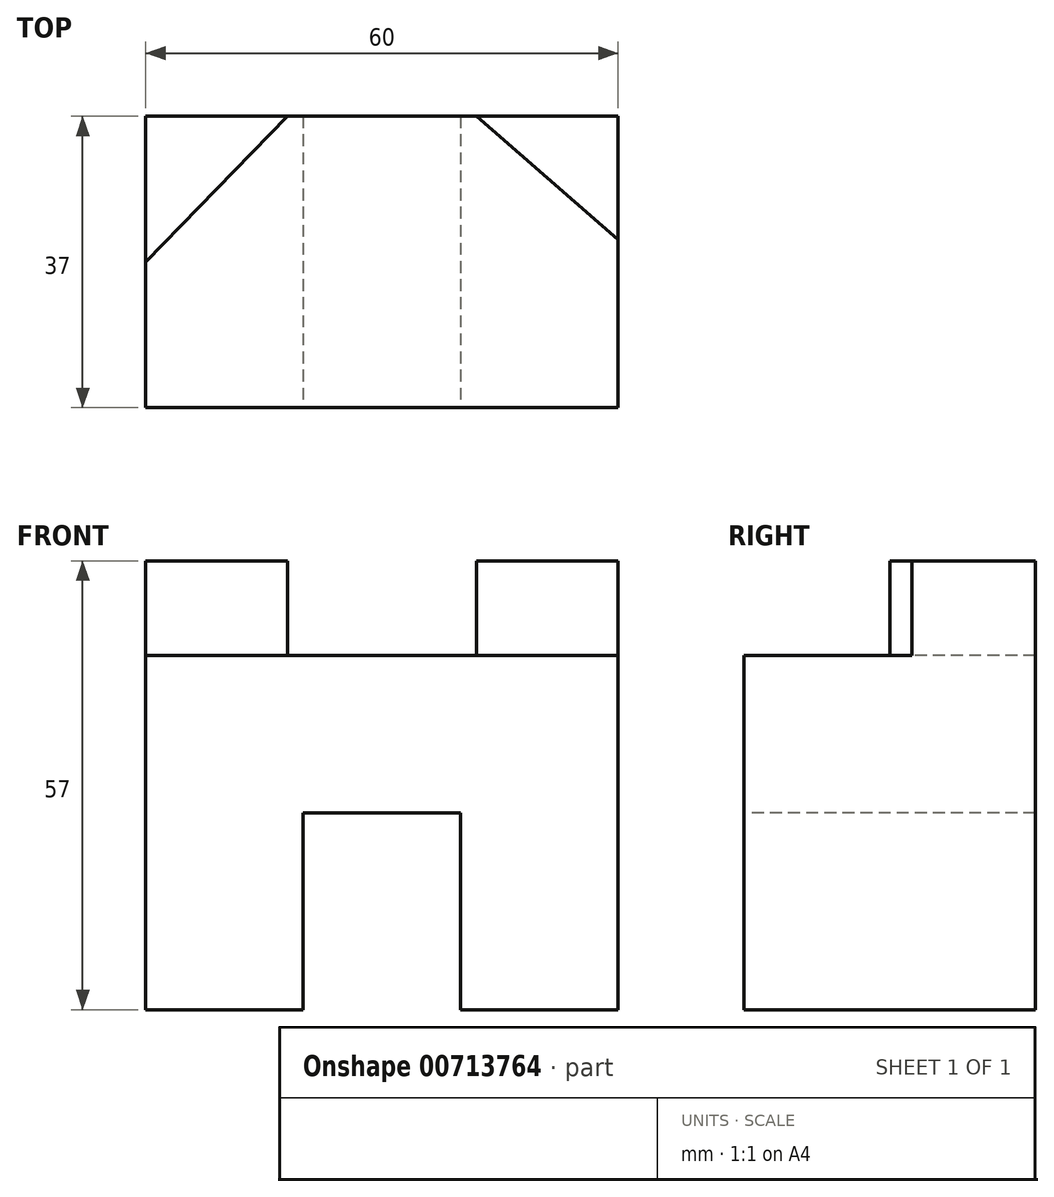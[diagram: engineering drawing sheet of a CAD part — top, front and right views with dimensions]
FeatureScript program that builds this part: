
annotation { "Feature Type Name" : "Feature", "Feature Type Description" : "" }
export const myFeature = defineFeature(function(context is Context, id is Id, definition is map)
    precondition{}
    {
        {
            var Q0;
            Q0=qCreatedBy(makeId("Front.planeOp"),FACE);
            var sketch = newSketch(context, id + "F0", { "sketchPlane" : qUnion([Q0])});
            skLineSegment(sketch, "E0.bottom", {"start": v(30, -28.5) * mm, "end": v(-30, -28.5) * mm});
            skLineSegment(sketch, "E0.top", {"start": v(30, 28.5) * mm, "end": v(-30, 28.5) * mm});
            skLineSegment(sketch, "E0.left", {"start": v(30, -28.5) * mm, "end": v(30, 28.5) * mm});
            skLineSegment(sketch, "E0.right", {"start": v(-30, -28.5) * mm, "end": v(-30, 28.5) * mm});
            skPoint(sketch, "E0.middle", {"position": v(0, 0) * mm});
            skLineSegment(sketch, "E1.left", {"start": v(12.78, -28.5) * mm, "end": v(12.78, -28.5) * mm});
            skLineSegment(sketch, "E1.right", {"start": v(-12.78, -28.5) * mm, "end": v(-12.78, -28.5) * mm});
            skPoint(sketch, "E1.middle", {"position": v(0, -28.5) * mm});
            skSolve(sketch);
        }
        {
            var Q0;
            Q0 = qSketchRegion(id + "F0", true);
            extrude(context, id + "F1", {"entities" : qUnion([Q0]), "depth" : 37 * mm, "offsetDistance" : 25 * mm});
        }
        {
            var Q0;
            Q0=makeQuery(id+"F1.opExtrude","SWEPT_FACE",FACE,{"disambiguationData":[OSD([sQuery(id+"F0.wireOp",EDGE,"E0.top")])]});
            var sketch = newSketch(context, id + "F2", { "sketchPlane" : qUnion([Q0])});
            skLineSegment(sketch, "E2", {"start": v(-12, 0) * mm, "end": v(-30, -18.5) * mm});
            skLineSegment(sketch, "E3", {"start": v(-30, -18.5) * mm, "end": v(-30, 0) * mm});
            skLineSegment(sketch, "E4", {"start": v(-30, 0) * mm, "end": v(-12, 0) * mm});
            skLineSegment(sketch, "E5", {"start": v(30, 0) * mm, "end": v(30, -15.7) * mm});
            skLineSegment(sketch, "E6", {"start": v(30, -15.7) * mm, "end": v(12, 0) * mm});
            skSolve(sketch);
        }
        {
            var Q0;
            {var subQ3=sQuery(id+"F2.wireOp",EDGE,"E2");Q0=makeQuery(id+"F2.imprint","IMPRINT",FACE,{"disambiguationData":[TD([[makeQuery(id+"F2.imprint","IMPRINT",EDGE,{"derivedFrom":subQ3}),1.0]])]});}
            extrude(context, id + "F3", {"entities" : qUnion([Q0]), "operationType" : NewBodyOperationType.REMOVE, "oppositeDirection" : true, "depth" : 12 * mm, "offsetDistance" : 25 * mm});
        }
        {
            var Q0;
            Q0=makeQuery(id+"F1.opExtrude","CAP_FACE",FACE,{"disambiguationData":[OSD([sQuery(id+"F0.wireOp",EDGE,"E0.bottom"),sQuery(id+"F0.wireOp",EDGE,"E0.top"),sQuery(id+"F0.wireOp",EDGE,"E0.left"),sQuery(id+"F0.wireOp",EDGE,"E0.right")])],"isStart":false});
            var sketch = newSketch(context, id + "F4", { "sketchPlane" : qUnion([Q0])});
            skLineSegment(sketch, "E7.bottom", {"start": v(10, -53.5) * mm, "end": v(-10, -53.5) * mm});
            skLineSegment(sketch, "E7.top", {"start": v(10, -3.5) * mm, "end": v(-10, -3.5) * mm});
            skLineSegment(sketch, "E7.left", {"start": v(10, -53.5) * mm, "end": v(10, -3.5) * mm});
            skLineSegment(sketch, "E7.right", {"start": v(-10, -53.5) * mm, "end": v(-10, -3.5) * mm});
            skPoint(sketch, "E7.middle", {"position": v(0, -28.5) * mm});
            skSolve(sketch);
        }
        {
            var Q0;
            Q0 = qSketchRegion(id + "F4", true);
            extrude(context, id + "F5", {"entities" : qUnion([Q0]), "operationType" : NewBodyOperationType.REMOVE, "endBound" : BoundingType.THROUGH_ALL, "oppositeDirection" : true, "depth" : 25 * mm, "offsetDistance" : 25 * mm});
        }
    });
